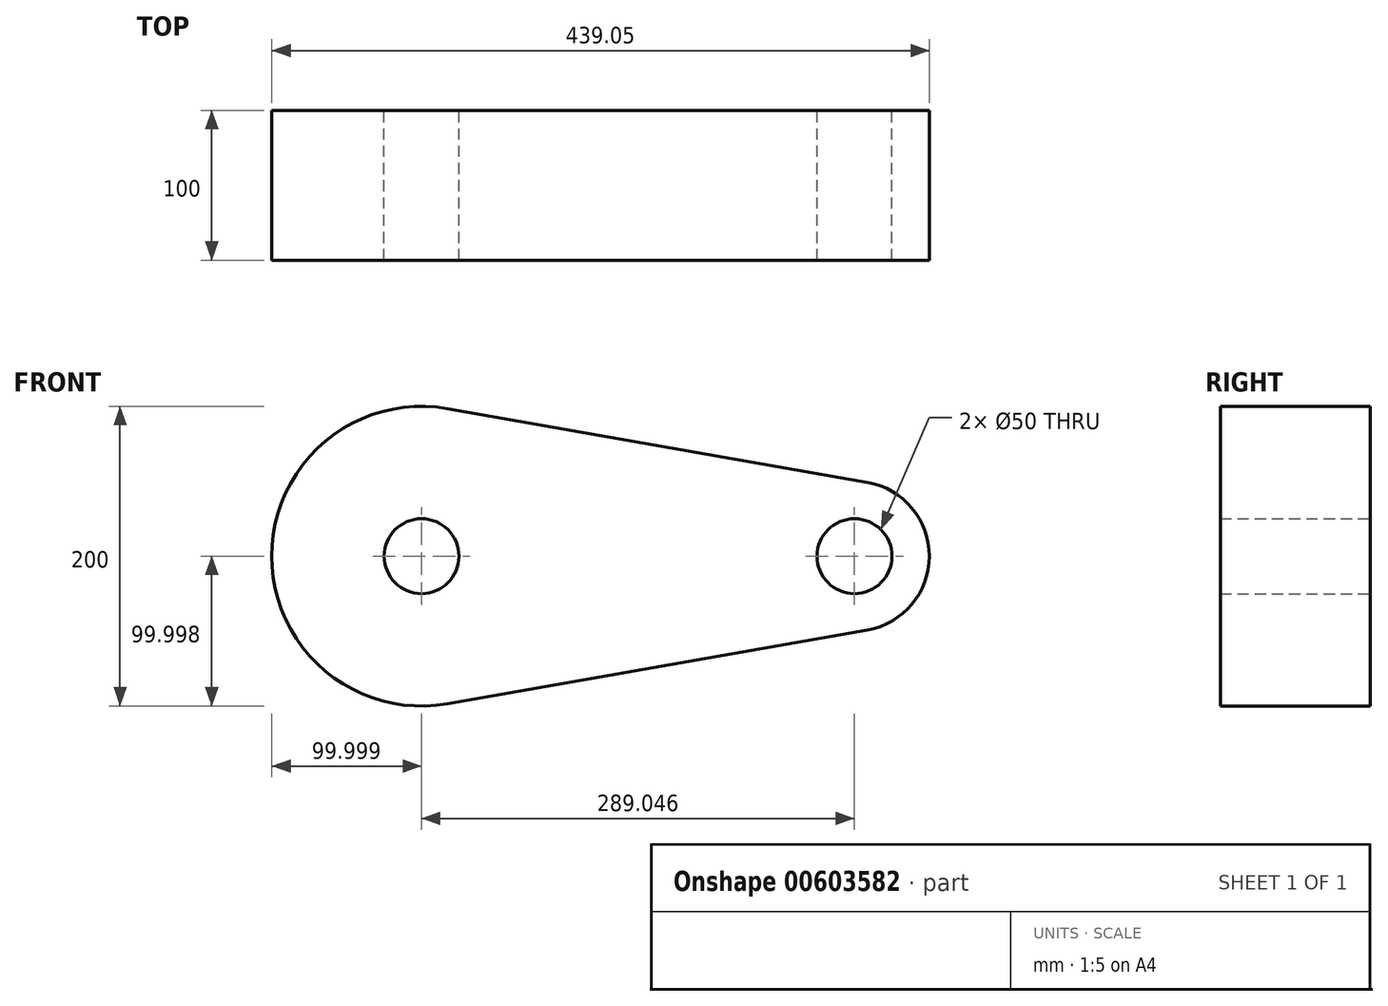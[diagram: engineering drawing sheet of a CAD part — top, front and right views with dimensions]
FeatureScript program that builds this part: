
annotation { "Feature Type Name" : "Feature", "Feature Type Description" : "" }
export const myFeature = defineFeature(function(context is Context, id is Id, definition is map)
    precondition{}
    {
        {
            var Q0;
            Q0=qCreatedBy(makeId("Front.planeOp"),FACE);
            var sketch = newSketch(context, id + "F0", { "sketchPlane" : qUnion([Q0])});
            skCircle(sketch, "E0", {"center": v(-126.91, 29.1) * mm, "radius": 100 * mm});
            skCircle(sketch, "E1", {"center": v(162.14, 29.1) * mm, "radius": 50 * mm});
            skCircle(sketch, "E2", {"center": v(-126.91, 29.1) * mm, "radius": 25 * mm});
            skCircle(sketch, "E3", {"center": v(162.14, 29.1) * mm, "radius": 25 * mm});
            skLineSegment(sketch, "E4", {"start": v(-109.61, 127.6) * mm, "end": v(170.78, 78.34) * mm});
            skLineSegment(sketch, "E5", {"start": v(-109.61, -69.4) * mm, "end": v(170.78, -20.15) * mm});
            skSolve(sketch);
        }
        {
            var Q0;
            Q0 = qSketchRegion(id + "F0", true);
            extrude(context, id + "F1", {"entities" : qUnion([Q0]), "depth" : 100 * mm, "offsetDistance" : 25 * mm});
        }
    });
